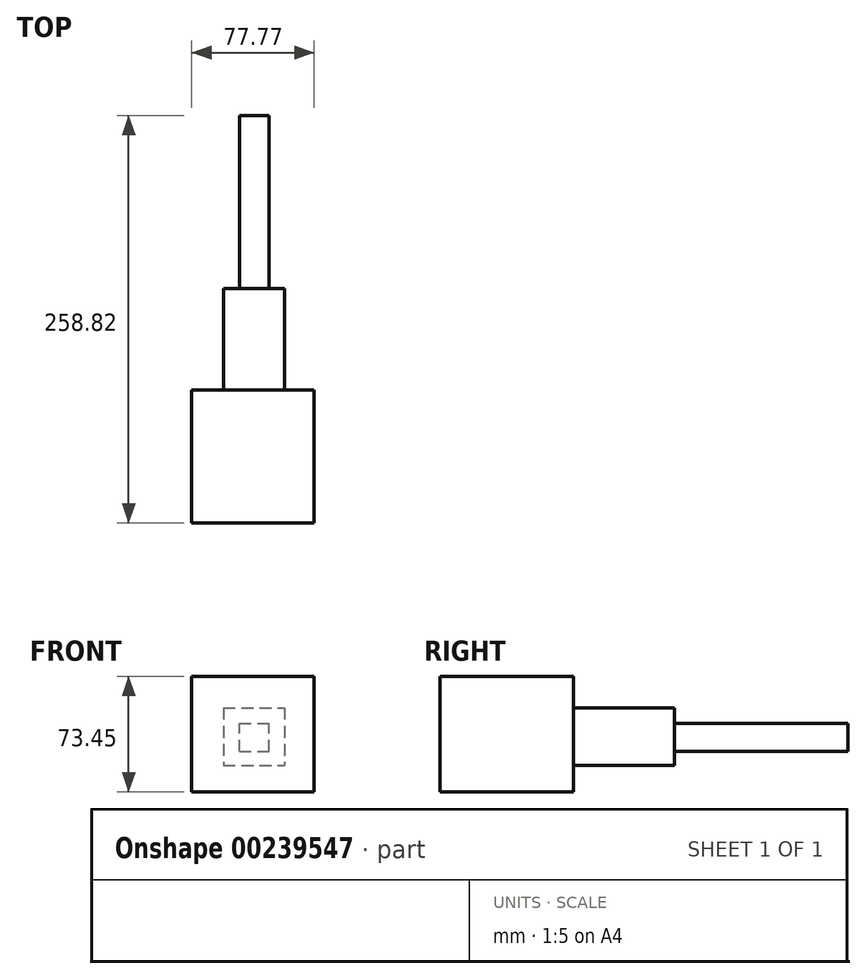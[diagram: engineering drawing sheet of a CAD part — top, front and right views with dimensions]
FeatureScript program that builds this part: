
annotation { "Feature Type Name" : "Feature", "Feature Type Description" : "" }
export const myFeature = defineFeature(function(context is Context, id is Id, definition is map)
    precondition{}
    {
        {
            var Q0;
            Q0=qCreatedBy(makeId("Front.planeOp"),FACE);
            var sketch = newSketch(context, id + "F0", { "sketchPlane" : qUnion([Q0])});
            skLineSegment(sketch, "E0.bottom", {"start": v(-39.15, 35.92) * mm, "end": v(38.62, 35.92) * mm});
            skLineSegment(sketch, "E0.top", {"start": v(-39.15, -37.53) * mm, "end": v(38.62, -37.53) * mm});
            skLineSegment(sketch, "E0.left", {"start": v(-39.15, 35.92) * mm, "end": v(-39.15, -37.53) * mm});
            skLineSegment(sketch, "E0.right", {"start": v(38.62, 35.92) * mm, "end": v(38.62, -37.53) * mm});
            skSolve(sketch);
        }
        {
            var Q0;
            Q0 = qSketchRegion(id + "F0", true);
            extrude(context, id + "F1", {"entities" : qUnion([Q0]), "endBound" : BoundingType.SYMMETRIC, "depth" : 84.58 * mm});
        }
        {
            var Q0;
            Q0=makeQuery(id+"F1.opExtrude","CAP_FACE",FACE,{"disambiguationData":[OSD([sQuery(id+"F0.wireOp",EDGE,"E0.bottom"),sQuery(id+"F0.wireOp",EDGE,"E0.top"),sQuery(id+"F0.wireOp",EDGE,"E0.left"),sQuery(id+"F0.wireOp",EDGE,"E0.right")])],"isStart":true});
            var sketch = newSketch(context, id + "F2", { "sketchPlane" : qUnion([Q0])});
            skSolve(sketch);
        }
        {
            var Q0;
            Q0=makeQuery(id+"F2.imprint","IMPRINT",FACE,{"disambiguationData":[TD([[makeQuery(id+"F2.imprint","IMPRINT",EDGE,{"derivedFrom":makeQuery(id+"F1.opExtrude","CAP_EDGE",EDGE,{"disambiguationData":[OSD([sQuery(id+"F0.wireOp",EDGE,"E0.bottom")])],"isStart":true})}),1.0]])]});
            var sketch = newSketch(context, id + "F3", { "sketchPlane" : qUnion([Q0])});
            skLineSegment(sketch, "E1.bottom", {"start": v(19.03, 15.98) * mm, "end": v(-19.63, 15.98) * mm});
            skLineSegment(sketch, "E1.top", {"start": v(19.03, -20.54) * mm, "end": v(-19.63, -20.54) * mm});
            skLineSegment(sketch, "E1.left", {"start": v(19.03, 15.98) * mm, "end": v(19.03, -20.54) * mm});
            skLineSegment(sketch, "E1.right", {"start": v(-19.63, 15.98) * mm, "end": v(-19.63, -20.54) * mm});
            skSolve(sketch);
        }
        {
            var Q0;
            Q0 = qSketchRegion(id + "F3", true);
            extrude(context, id + "F4", {"entities" : qUnion([Q0]), "operationType" : NewBodyOperationType.ADD, "depth" : 64.26 * mm});
        }
        {
            var Q0;
            Q0=makeQuery(id+"F4.opExtrude","CAP_FACE",FACE,{"disambiguationData":[OSD([sQuery(id+"F3.wireOp",EDGE,"E1.bottom"),sQuery(id+"F3.wireOp",EDGE,"E1.top"),sQuery(id+"F3.wireOp",EDGE,"E1.left"),sQuery(id+"F3.wireOp",EDGE,"E1.right")])],"isStart":false});
            var sketch = newSketch(context, id + "F5", { "sketchPlane" : qUnion([Q0])});
            skLineSegment(sketch, "E2.bottom", {"start": v(8.96, -11.76) * mm, "end": v(-9.99, -11.76) * mm});
            skLineSegment(sketch, "E2.top", {"start": v(8.96, 6) * mm, "end": v(-9.99, 6) * mm});
            skLineSegment(sketch, "E2.left", {"start": v(8.96, -11.76) * mm, "end": v(8.96, 6) * mm});
            skLineSegment(sketch, "E2.right", {"start": v(-9.99, -11.76) * mm, "end": v(-9.99, 6) * mm});
            skSolve(sketch);
        }
        {
            var Q0;
            Q0 = qSketchRegion(id + "F5", true);
            extrude(context, id + "F6", {"entities" : qUnion([Q0]), "operationType" : NewBodyOperationType.ADD, "depth" : 109.98 * mm});
        }
    });
